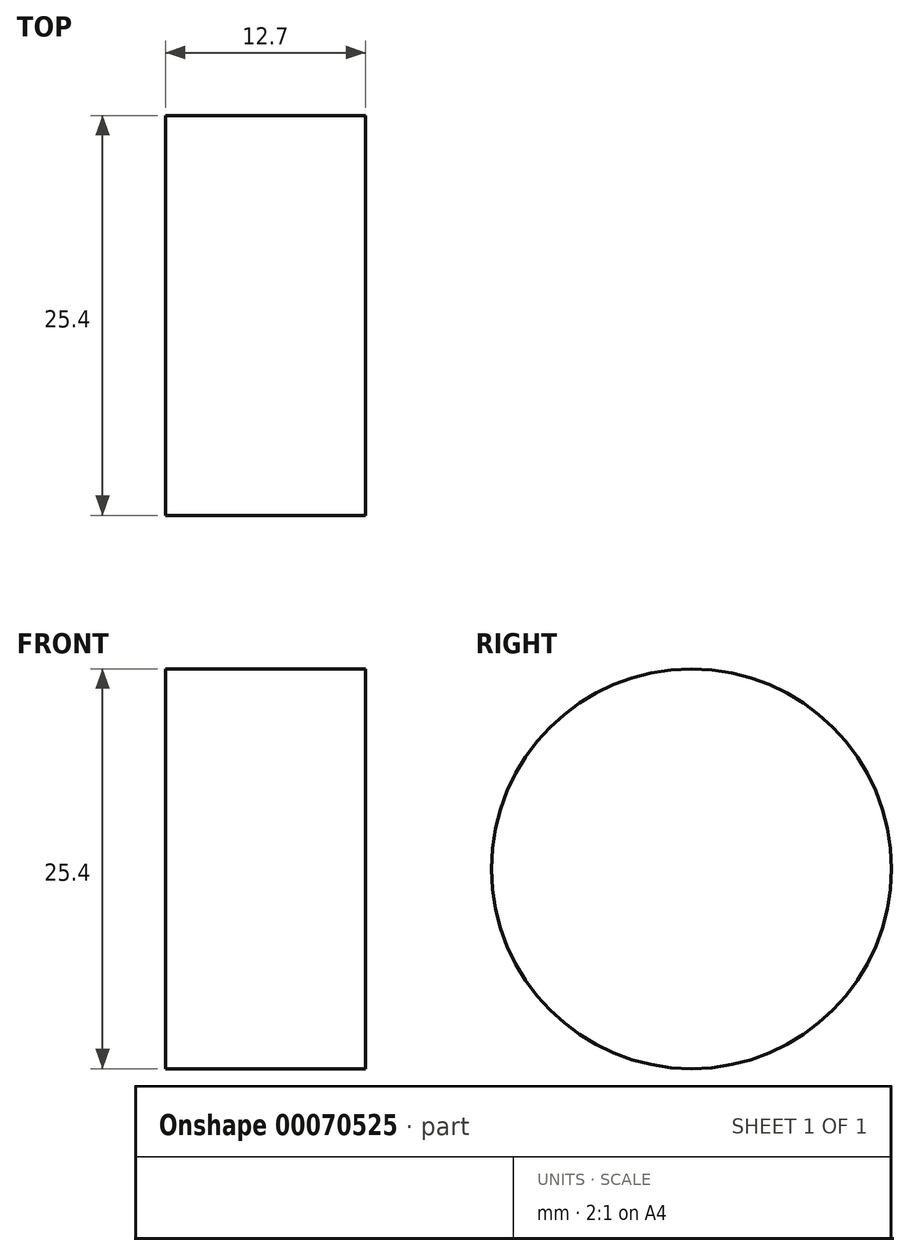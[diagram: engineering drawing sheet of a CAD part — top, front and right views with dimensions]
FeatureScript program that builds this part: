
annotation { "Feature Type Name" : "Feature", "Feature Type Description" : "" }
export const myFeature = defineFeature(function(context is Context, id is Id, definition is map)
    precondition{}
    {
        {
            var Q0;
            Q0=qCreatedBy(makeId("Right.planeOp"),FACE);
            var sketch = newSketch(context, id + "F0", { "sketchPlane" : qUnion([Q0])});
            skCircle(sketch, "E0", {"center": v(0, 0) * mm, "radius": 12.7 * mm});
            skSolve(sketch);
        }
        {
            var Q0;
            Q0=makeQuery(id+"F0.imprint","IMPRINT",FACE,{"disambiguationData":[TD([[makeQuery(id+"F0.imprint","IMPRINT",EDGE,{"derivedFrom":sQuery(id+"F0.wireOp",EDGE,"E0")}),1.0]])]});
            extrude(context, id + "F1", {"entities" : qUnion([Q0]), "depth" : 12.7 * mm});
        }
    });
